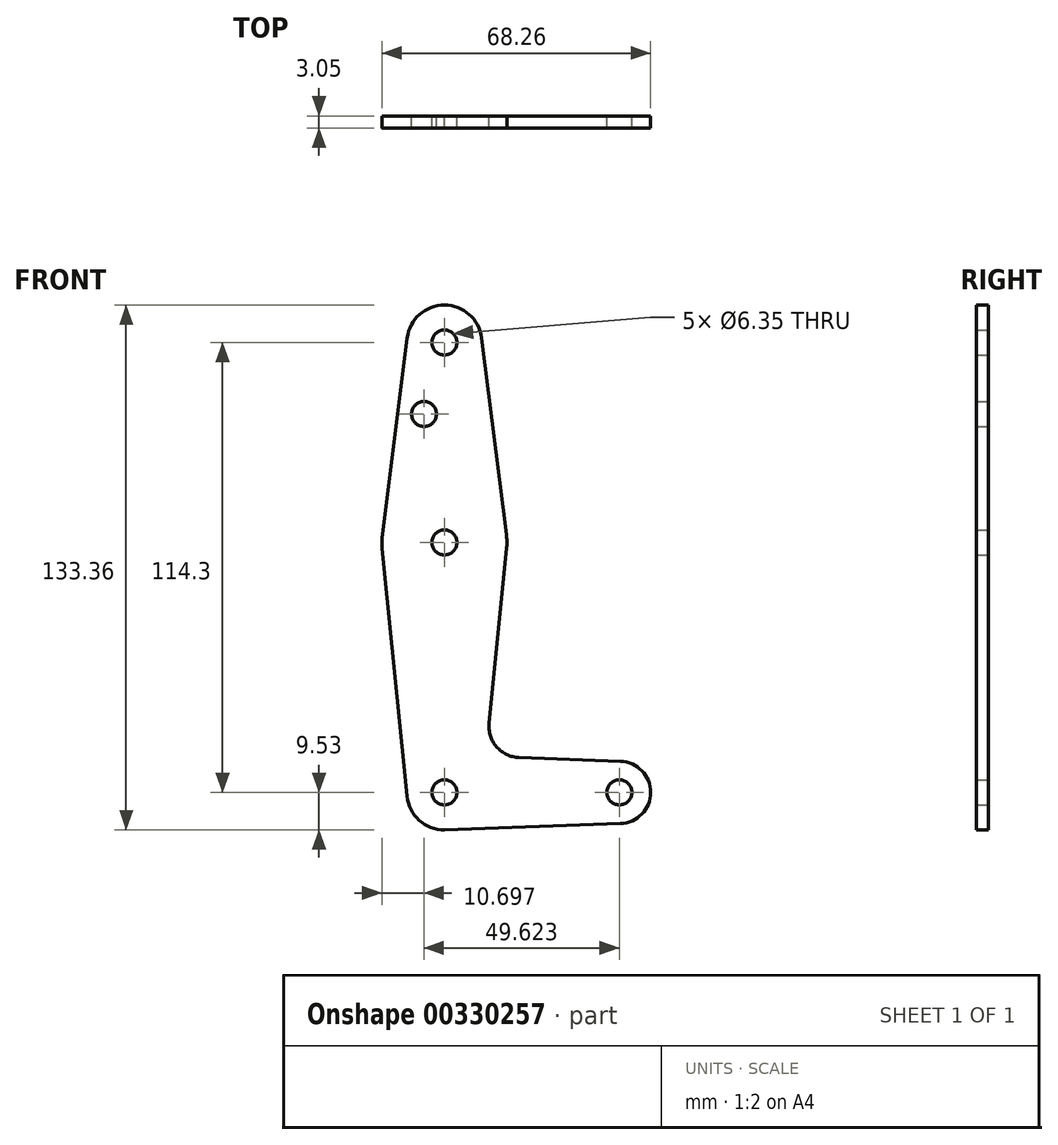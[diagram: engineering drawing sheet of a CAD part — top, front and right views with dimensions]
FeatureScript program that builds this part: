
annotation { "Feature Type Name" : "Feature", "Feature Type Description" : "" }
export const myFeature = defineFeature(function(context is Context, id is Id, definition is map)
    precondition{}
    {
        {
            var Q0;
            Q0=qCreatedBy(makeId("Front.planeOp"),FACE);
            var sketch = newSketch(context, id + "F0", { "sketchPlane" : qUnion([Q0])});
            skLineSegment(sketch, "E0", {"start": v(0, 114.3) * mm, "end": v(0, 63.5) * mm, "construction": true});
            skLineSegment(sketch, "E1", {"start": v(0, 63.5) * mm, "end": v(0, 0) * mm, "construction": true});
            skLineSegment(sketch, "E2", {"start": v(0, 0) * mm, "end": v(44.45, 0) * mm, "construction": true});
            skCircle(sketch, "E3", {"center": v(0, 114.3) * mm, "radius": 9.53 * mm});
            skCircle(sketch, "E4", {"center": v(0, 63.5) * mm, "radius": 15.88 * mm});
            skCircle(sketch, "E5", {"center": v(0, 0) * mm, "radius": 9.53 * mm});
            skCircle(sketch, "E6", {"center": v(44.45, 0) * mm, "radius": 7.94 * mm});
            skLineSegment(sketch, "E7", {"start": v(0, -9.53) * mm, "end": v(44.73, -7.93) * mm});
            skLineSegment(sketch, "E8", {"start": v(-9.45, 115.5) * mm, "end": v(-15.75, 65.48) * mm});
            skLineSegment(sketch, "E9", {"start": v(15.75, 65.48) * mm, "end": v(9.45, 115.5) * mm});
            skLineSegment(sketch, "E10", {"start": v(44.73, 7.93) * mm, "end": v(18.97, 8.85) * mm});
            skLineSegment(sketch, "E11", {"start": v(15.8, 61.91) * mm, "end": v(11.34, 17.6) * mm});
            skLineSegment(sketch, "E12", {"start": v(-15.8, 61.91) * mm, "end": v(-9.48, -0.95) * mm});
            skArc(sketch, "E13.filletArc", {"start": v(11.34, 17.6) * mm, "mid": v(13.26, 11.57) * mm, "end": v(18.97, 8.85) * mm});
            skCircle(sketch, "E14", {"center": v(0, 114.3) * mm, "radius": 3.18 * mm});
            skCircle(sketch, "E15", {"center": v(0, 63.5) * mm, "radius": 3.18 * mm});
            skCircle(sketch, "E16", {"center": v(0, 0) * mm, "radius": 3.18 * mm});
            skCircle(sketch, "E17", {"center": v(44.45, 0) * mm, "radius": 3.18 * mm});
            skCircle(sketch, "E18", {"center": v(-5.17, 96.14) * mm, "radius": 3.18 * mm});
            skSolve(sketch);
        }
        {
            var Q0;
            Q0=makeQuery(id+"F0.imprint","IMPRINT",FACE,{"disambiguationData":[TD([[makeQuery(id+"F0.imprint","IMPRINT",EDGE,{"derivedFrom":sQuery(id+"F0.wireOp",EDGE,"E14")}),-1.0]])]});
            var Q1;
            {var subQ1=sQuery(id+"F0.wireOp",EDGE,"E8");Q1=makeQuery(id+"F0.imprint","IMPRINT",FACE,{"disambiguationData":[TD([[makeQuery(id+"F0.imprint","IMPRINT",EDGE,{"derivedFrom":subQ1}),1.0]])]});}
            var Q2;
            Q2=makeQuery(id+"F0.imprint","IMPRINT",FACE,{"disambiguationData":[TD([[makeQuery(id+"F0.imprint","IMPRINT",EDGE,{"derivedFrom":sQuery(id+"F0.wireOp",EDGE,"E15")}),-1.0]])]});
            var Q3;
            {var subQ6=sQuery(id+"F0.wireOp",EDGE,"E10");Q3=makeQuery(id+"F0.imprint","IMPRINT",FACE,{"disambiguationData":[TD([[makeQuery(id+"F0.imprint","IMPRINT",EDGE,{"derivedFrom":subQ6}),1.0]])]});}
            var Q4;
            Q4=makeQuery(id+"F0.imprint","IMPRINT",FACE,{"disambiguationData":[TD([[makeQuery(id+"F0.imprint","IMPRINT",EDGE,{"derivedFrom":sQuery(id+"F0.wireOp",EDGE,"E16")}),-1.0]])]});
            var Q5;
            Q5=makeQuery(id+"F0.imprint","IMPRINT",FACE,{"disambiguationData":[TD([[makeQuery(id+"F0.imprint","IMPRINT",EDGE,{"derivedFrom":sQuery(id+"F0.wireOp",EDGE,"E17")}),-1.0]])]});
            extrude(context, id + "F1", {"entities" : qUnion([Q0, Q1, Q2, Q3, Q4, Q5]), "depth" : 3.05 * mm});
        }
    });
